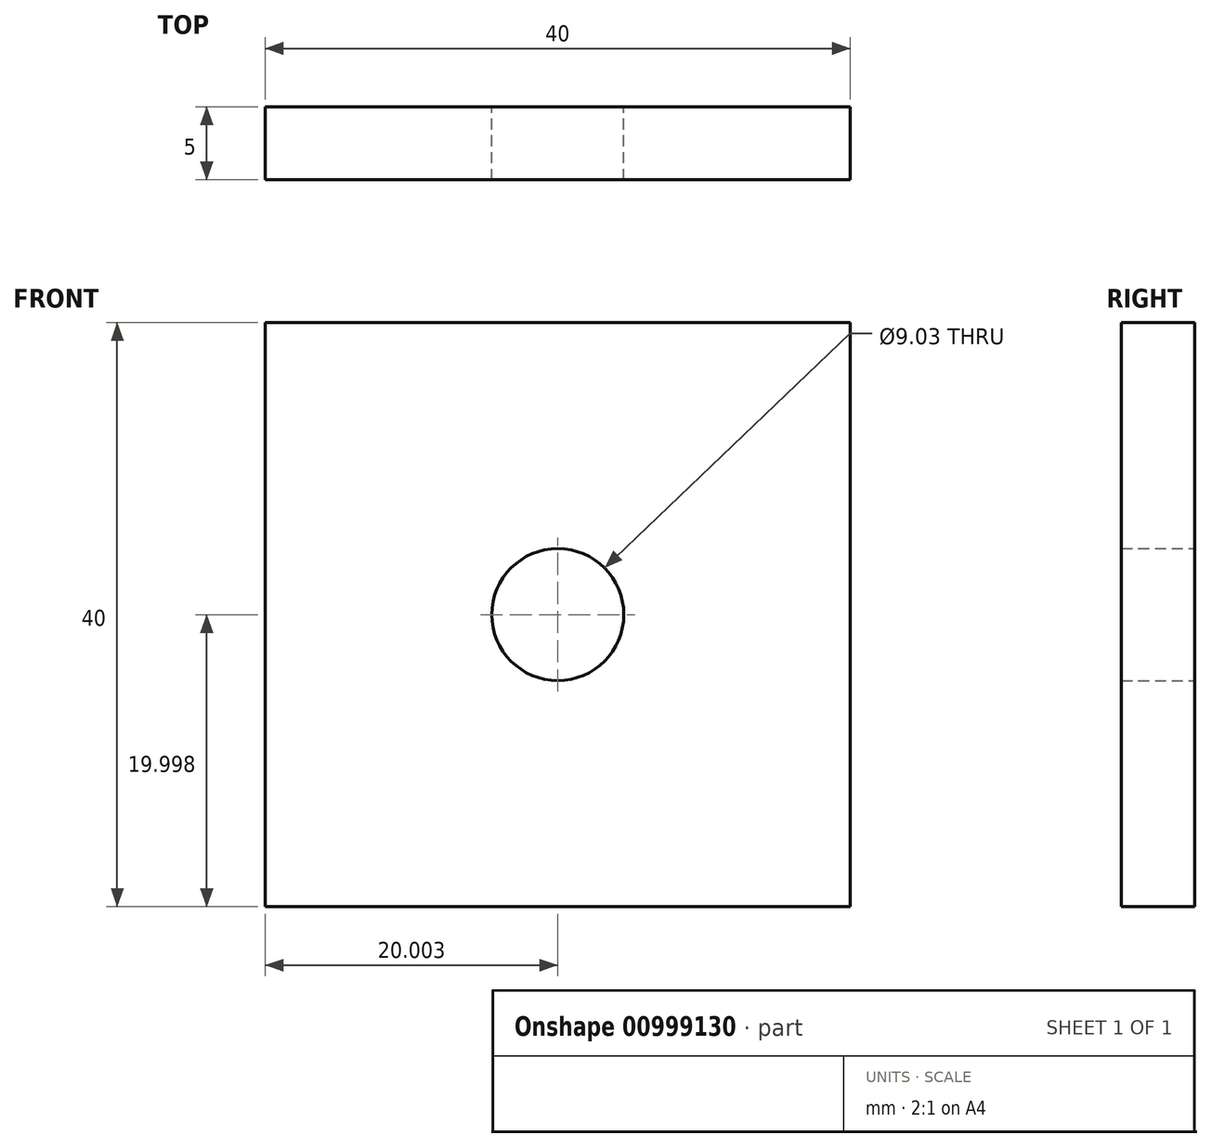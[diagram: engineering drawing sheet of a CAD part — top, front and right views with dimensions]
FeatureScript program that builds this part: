
annotation { "Feature Type Name" : "Feature", "Feature Type Description" : "" }
export const myFeature = defineFeature(function(context is Context, id is Id, definition is map)
    precondition{}
    {
        {
            var Q0;
            Q0=qCreatedBy(makeId("Front.planeOp"),FACE);
            var sketch = newSketch(context, id + "F0", { "sketchPlane" : qUnion([Q0])});
            skLineSegment(sketch, "E0.bottom", {"start": v(-22.43, 17.72) * mm, "end": v(17.57, 17.72) * mm});
            skLineSegment(sketch, "E0.top", {"start": v(-22.43, -22.28) * mm, "end": v(17.57, -22.28) * mm});
            skLineSegment(sketch, "E0.left", {"start": v(-22.43, 17.72) * mm, "end": v(-22.43, -22.28) * mm});
            skLineSegment(sketch, "E0.right", {"start": v(17.57, 17.72) * mm, "end": v(17.57, -22.28) * mm});
            skPoint(sketch, "E1", {"position": v(-22.43, -2.28) * mm});
            skPoint(sketch, "E2", {"position": v(-2.43, -22.28) * mm});
            skLineSegment(sketch, "E3", {"start": v(-22.43, -2.28) * mm, "end": v(30.52, -2.28) * mm, "construction": true});
            skLineSegment(sketch, "E4", {"start": v(-2.43, -22.28) * mm, "end": v(-2.43, 25.7) * mm, "construction": true});
            skCircle(sketch, "E5", {"center": v(-2.43, -2.28) * mm, "radius": 4.52 * mm});
            skSolve(sketch);
        }
        {
            var Q0;
            Q0 = qSketchRegion(id + "F0", true);
            extrude(context, id + "F1", {"entities" : qUnion([Q0]), "depth" : 5 * mm, "offsetDistance" : 25 * mm});
        }
    });
